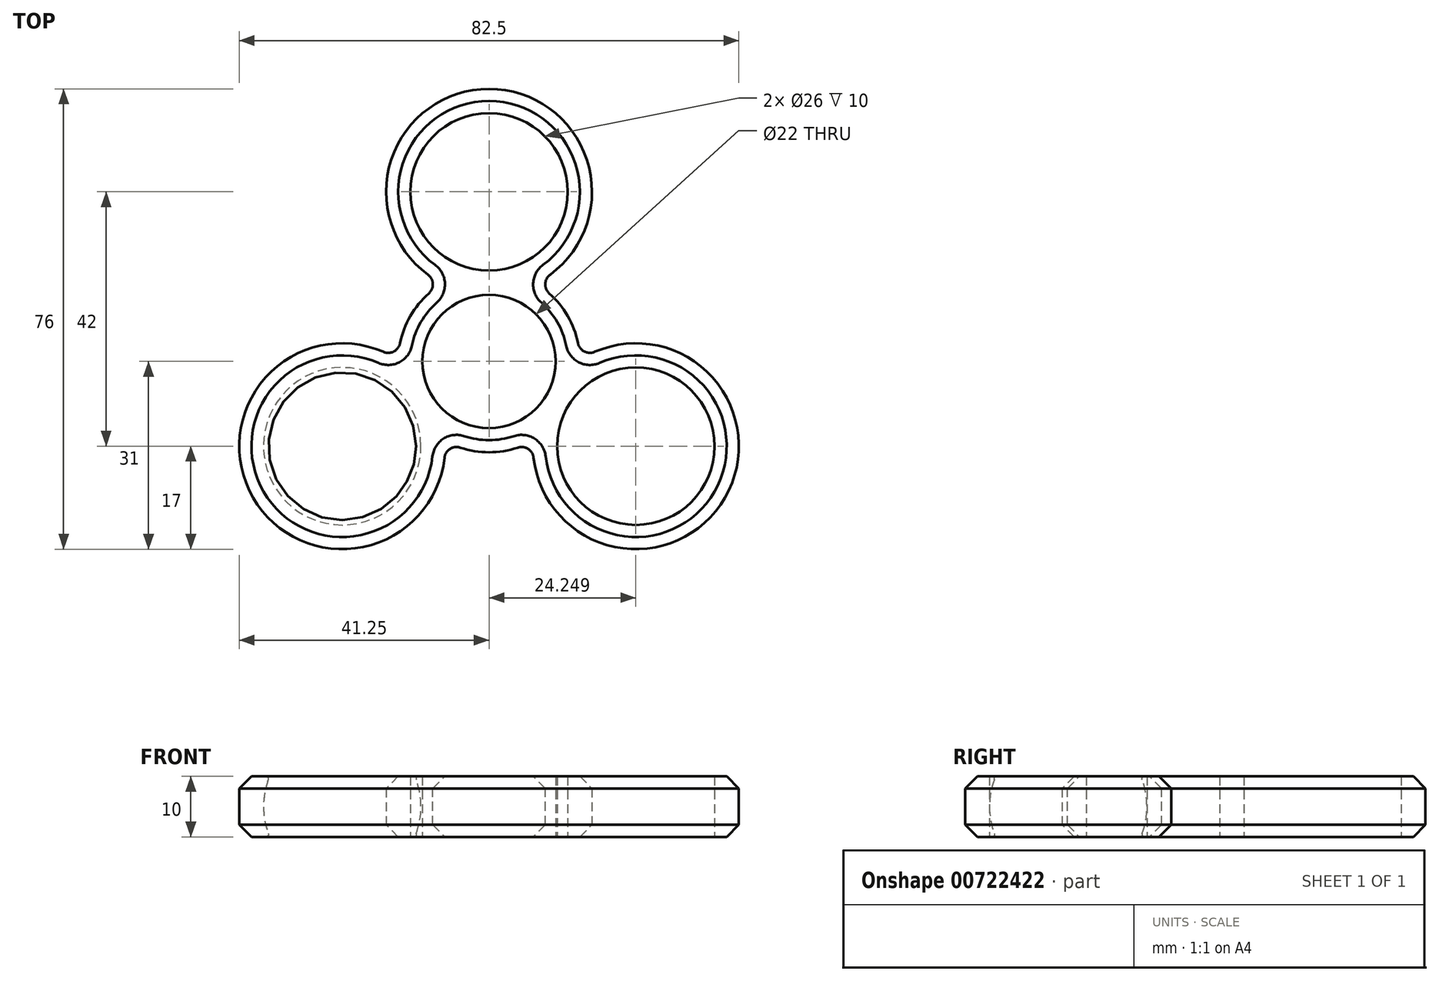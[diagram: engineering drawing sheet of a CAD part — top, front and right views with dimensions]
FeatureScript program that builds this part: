
annotation { "Feature Type Name" : "Feature", "Feature Type Description" : "" }
export const myFeature = defineFeature(function(context is Context, id is Id, definition is map)
    precondition{}
    {
        {
            var Q0;
            Q0=qCreatedBy(makeId("Top.planeOp"),FACE);
            var sketch = newSketch(context, id + "F0", { "sketchPlane" : qUnion([Q0])});
            skLineSegment(sketch, "E0", {"start": v(0, 0) * mm, "end": v(0, 28) * mm, "construction": true});
            skCircle(sketch, "E1", {"center": v(0, 28) * mm, "radius": 13 * mm});
            skArc(sketch, "E2", {"start": v(7.73, 12.86) * mm, "mid": v(0, 45) * mm, "end": v(-7.73, 12.86) * mm});
            skCircle(sketch, "E3", {"center": v(0, 0) * mm, "radius": 11 * mm});
            skArc(sketch, "E4", {"start": v(-7.27, -13.12) * mm, "mid": v(0, -15) * mm, "end": v(7.27, -13.12) * mm});
            skArc(sketch, "E5.1.2", {"start": v(-15, 0.26) * mm, "mid": v(-38.97, -22.5) * mm, "end": v(-7.27, -13.12) * mm});
            skCircle(sketch, "E5.1.3", {"center": v(-24.25, -14) * mm, "radius": 13 * mm});
            skArc(sketch, "E5.2.2", {"start": v(7.27, -13.12) * mm, "mid": v(38.97, -22.5) * mm, "end": v(15, 0.26) * mm});
            skCircle(sketch, "E5.2.3", {"center": v(24.25, -14) * mm, "radius": 13 * mm});
            skArc(sketch, "E6.trimOffspring", {"start": v(15, 0.26) * mm, "mid": v(13, 7.5) * mm, "end": v(7.73, 12.86) * mm});
            skArc(sketch, "E7.trimOffspring", {"start": v(-7.73, 12.86) * mm, "mid": v(-13, 7.5) * mm, "end": v(-15, 0.26) * mm});
            skLineSegment(sketch, "E8", {"start": v(0, 0) * mm, "end": v(-24.25, -14) * mm, "construction": true});
            skLineSegment(sketch, "E9", {"start": v(0, 0) * mm, "end": v(24.25, -14) * mm, "construction": true});
            skSolve(sketch);
        }
        {
            var Q0;
            Q0=qSketchRegion(id+"F0",true);
            extrude(context, id + "F1", {"entities" : qUnion([Q0]), "depth" : 10 * mm, "offsetDistance" : 25 * mm});
        }
        {
            var Q0;
            Q0=makeQuery(id+"F1.opExtrude","SWEPT_EDGE",EDGE,{"disambiguationData":[OSD([sQuery(id+"F0.wireOp",EDGE,"E4"),sQuery(id+"F0.wireOp",EDGE,"E5.1.2")])]});
            var Q1;
            Q1=makeQuery(id+"F1.opExtrude","SWEPT_EDGE",EDGE,{"disambiguationData":[OSD([sQuery(id+"F0.wireOp",EDGE,"E4"),sQuery(id+"F0.wireOp",EDGE,"E5.2.2")])]});
            var Q2;
            Q2=makeQuery(id+"F1.opExtrude","SWEPT_EDGE",EDGE,{"disambiguationData":[OSD([sQuery(id+"F0.wireOp",EDGE,"E5.2.2"),sQuery(id+"F0.wireOp",EDGE,"E6.trimOffspring")])]});
            var Q3;
            Q3=makeQuery(id+"F1.opExtrude","SWEPT_EDGE",EDGE,{"disambiguationData":[OSD([sQuery(id+"F0.wireOp",EDGE,"E2"),sQuery(id+"F0.wireOp",EDGE,"E6.trimOffspring")])]});
            var Q4;
            Q4=makeQuery(id+"F1.opExtrude","SWEPT_EDGE",EDGE,{"disambiguationData":[OSD([sQuery(id+"F0.wireOp",EDGE,"E2"),sQuery(id+"F0.wireOp",EDGE,"E7.trimOffspring")])]});
            var Q5;
            Q5=makeQuery(id+"F1.opExtrude","SWEPT_EDGE",EDGE,{"disambiguationData":[OSD([sQuery(id+"F0.wireOp",EDGE,"E5.1.2"),sQuery(id+"F0.wireOp",EDGE,"E7.trimOffspring")])]});
            fillet(context, id + "F2", {"entities" : qUnion([Q0, Q1, Q2, Q3, Q4, Q5]), "radius" : 2 * mm, "tangentPropagation" : true, "allowEdgeOverflow" : false});
        }
        {
            var Q0;
            Q0=makeQuery(id+"F1.opExtrude","CAP_EDGE",EDGE,{"disambiguationData":[OSD([sQuery(id+"F0.wireOp",EDGE,"E5.2.2")])],"isStart":true});
            var Q1;
            Q1=makeQuery(id+"F1.opExtrude","CAP_EDGE",EDGE,{"disambiguationData":[OSD([sQuery(id+"F0.wireOp",EDGE,"E5.2.2")])],"isStart":false});
            chamfer(context, id + "F3", {"entities" : qUnion([Q0, Q1]), "width" : 2 * mm, "tangentPropagation" : true});
        }
        {
            var Q0;
            Q0=qCreatedBy(makeId("Top.planeOp"),FACE);
            var sketch = newSketch(context, id + "F4", { "sketchPlane" : qUnion([Q0])});
            skCircle(sketch, "E10.0", {"center": v(-24.25, -14) * mm, "radius": 13 * mm, "construction": true});
            skLineSegment(sketch, "E11", {"start": v(0, 0) * mm, "end": v(-24.25, -14) * mm, "construction": true});
            skCircle(sketch, "E12.0", {"center": v(0, 28) * mm, "radius": 13 * mm, "construction": true});
            skLineSegment(sketch, "E13", {"start": v(0, 0) * mm, "end": v(0, 28) * mm, "construction": true});
            skCircle(sketch, "E14.0", {"center": v(24.25, -14) * mm, "radius": 13 * mm, "construction": true});
            skLineSegment(sketch, "E15", {"start": v(0, 0) * mm, "end": v(24.25, -14) * mm, "construction": true});
            skSolve(sketch);
        }
        {
            var Q0;
            {var subQ0=sQuery(id+"F0.wireOp",EDGE,"E5.1.2");Q0=makeQuery(id+"F3.opChamfer","BLEND_EDGE",EDGE,{"blendedFrom":[makeQuery(id+"F1.opExtrude","CAP_EDGE",EDGE,{"disambiguationData":[OSD([subQ0])],"isStart":false}),makeQuery(id+"F1.opExtrude","CAP_FACE",FACE,{"disambiguationData":[OSD([sQuery(id+"F0.wireOp",EDGE,"E1"),sQuery(id+"F0.wireOp",EDGE,"E2"),sQuery(id+"F0.wireOp",EDGE,"E3"),sQuery(id+"F0.wireOp",EDGE,"E4"),subQ0,sQuery(id+"F0.wireOp",EDGE,"E5.1.3"),sQuery(id+"F0.wireOp",EDGE,"E5.2.2"),sQuery(id+"F0.wireOp",EDGE,"E5.2.3"),sQuery(id+"F0.wireOp",EDGE,"E6.trimOffspring"),sQuery(id+"F0.wireOp",EDGE,"E7.trimOffspring")])],"isStart":false})],"blendedInto":[makeQuery(id+"F1.opExtrude","CAP_FACE",FACE,{"disambiguationData":[OSD([sQuery(id+"F0.wireOp",EDGE,"E1"),sQuery(id+"F0.wireOp",EDGE,"E2"),sQuery(id+"F0.wireOp",EDGE,"E3"),sQuery(id+"F0.wireOp",EDGE,"E4"),subQ0,sQuery(id+"F0.wireOp",EDGE,"E5.1.3"),sQuery(id+"F0.wireOp",EDGE,"E5.2.2"),sQuery(id+"F0.wireOp",EDGE,"E5.2.3"),sQuery(id+"F0.wireOp",EDGE,"E6.trimOffspring"),sQuery(id+"F0.wireOp",EDGE,"E7.trimOffspring")])],"isStart":false})]});}
            cPoint(context, id + "F5", {"entities" : qUnion([Q0]), "parameter" : 0.5});
        }
        {
            var Q0;
            Q0=sQuery(id+"F4.wireOp",VERTEX,"E11.start");
            var Q1;
            Q1=sQuery(id+"F4.wireOp",VERTEX,"E10.0.center");
            var Q2;
            Q2=qCreatedBy(id+"F5",VERTEX);
            cPlane(context, id + "F6", {"entities" : qUnion([Q0, Q1, Q2]), "cplaneType" : CPlaneType.THREE_POINT, "offset" : 25 * mm, "width" : 150 * mm, "height" : 150 * mm});
        }
        {
            var Q0;
            Q0=qCreatedBy(id+"F6.planeOp",FACE);
            var sketch = newSketch(context, id + "F7", { "sketchPlane" : qUnion([Q0])});
            skLineSegment(sketch, "E16.0", {"start": v(-41, 10) * mm, "end": v(-40, 10) * mm, "construction": true});
            skLineSegment(sketch, "E17.1", {"start": v(-41, 0) * mm, "end": v(-40, 0) * mm, "construction": true});
            skLineSegment(sketch, "E18", {"start": v(-41, 10) * mm, "end": v(-41, 0) * mm});
            skLineSegment(sketch, "E19", {"start": v(-28, 0) * mm, "end": v(-28, 10) * mm, "construction": true});
            skArc(sketch, "E20", {"start": v(-40, 10) * mm, "mid": v(-41, 5) * mm, "end": v(-40, 0) * mm});
            skLineSegment(sketch, "E21", {"start": v(-41, 10) * mm, "end": v(-40, 10) * mm});
            skLineSegment(sketch, "E22", {"start": v(-41, 0) * mm, "end": v(-40, 0) * mm});
            skLineSegment(sketch, "E23.trimOffspring", {"start": v(-28, 10) * mm, "end": v(-15, 10) * mm, "construction": true});
            skLineSegment(sketch, "E24.trimOffspring", {"start": v(-28, 0) * mm, "end": v(-15, 0) * mm, "construction": true});
            skSolve(sketch);
        }
        {
            var Q0;
            Q0=qSketchRegion(id+"F7",true);
            var Q1;
            Q1=sQuery(id+"F7.wireOp",EDGE,"E19");
            revolve(context, id + "F8", {"operationType" : NewBodyOperationType.ADD, "surfaceOperationType" : NewSurfaceOperationType.NEW, "entities" : qUnion([Q0]), "axis" : qUnion([Q1]), "revolveType" : RevolveType.FULL});
        }
        {
            var Q0;
            Q0=makeQuery(id+"F8.opRevolve","SWEPT_EDGE",EDGE,{"disambiguationData":[OSD([sQuery(id+"F7.wireOp",EDGE,"E20"),sQuery(id+"F7.wireOp",EDGE,"E21")])]});
            var Q1;
            Q1=makeQuery(id+"F8.opRevolve","SWEPT_EDGE",EDGE,{"disambiguationData":[OSD([sQuery(id+"F7.wireOp",EDGE,"E20"),sQuery(id+"F7.wireOp",EDGE,"E22")])]});
            var Q2;
            Q2=makeQuery(id+"FEcUt43eDZ80vxZ_1.2.F8.opRevolve","SWEPT_EDGE",EDGE,{"disambiguationData":[OSD([sQuery(id+"F7.wireOp",EDGE,"E20"),sQuery(id+"F7.wireOp",EDGE,"E21")])]});
            var Q3;
            Q3=makeQuery(id+"FEcUt43eDZ80vxZ_1.2.F8.opRevolve","SWEPT_EDGE",EDGE,{"disambiguationData":[OSD([sQuery(id+"F7.wireOp",EDGE,"E20"),sQuery(id+"F7.wireOp",EDGE,"E22")])]});
            var Q4;
            Q4=makeQuery(id+"Fynh9oEJvHPlE7w_1.2.F8.opRevolve","SWEPT_EDGE",EDGE,{"disambiguationData":[OSD([sQuery(id+"F7.wireOp",EDGE,"E20"),sQuery(id+"F7.wireOp",EDGE,"E21")])]});
            var Q5;
            Q5=makeQuery(id+"Fynh9oEJvHPlE7w_1.2.F8.opRevolve","SWEPT_EDGE",EDGE,{"disambiguationData":[OSD([sQuery(id+"F7.wireOp",EDGE,"E20"),sQuery(id+"F7.wireOp",EDGE,"E22")])]});
            fillet(context, id + "F9", {"entities" : qUnion([Q0, Q1, Q2, Q3, Q4, Q5]), "radius" : .4 * mm, "tangentPropagation" : true, "allowEdgeOverflow" : false});
        }
    });
